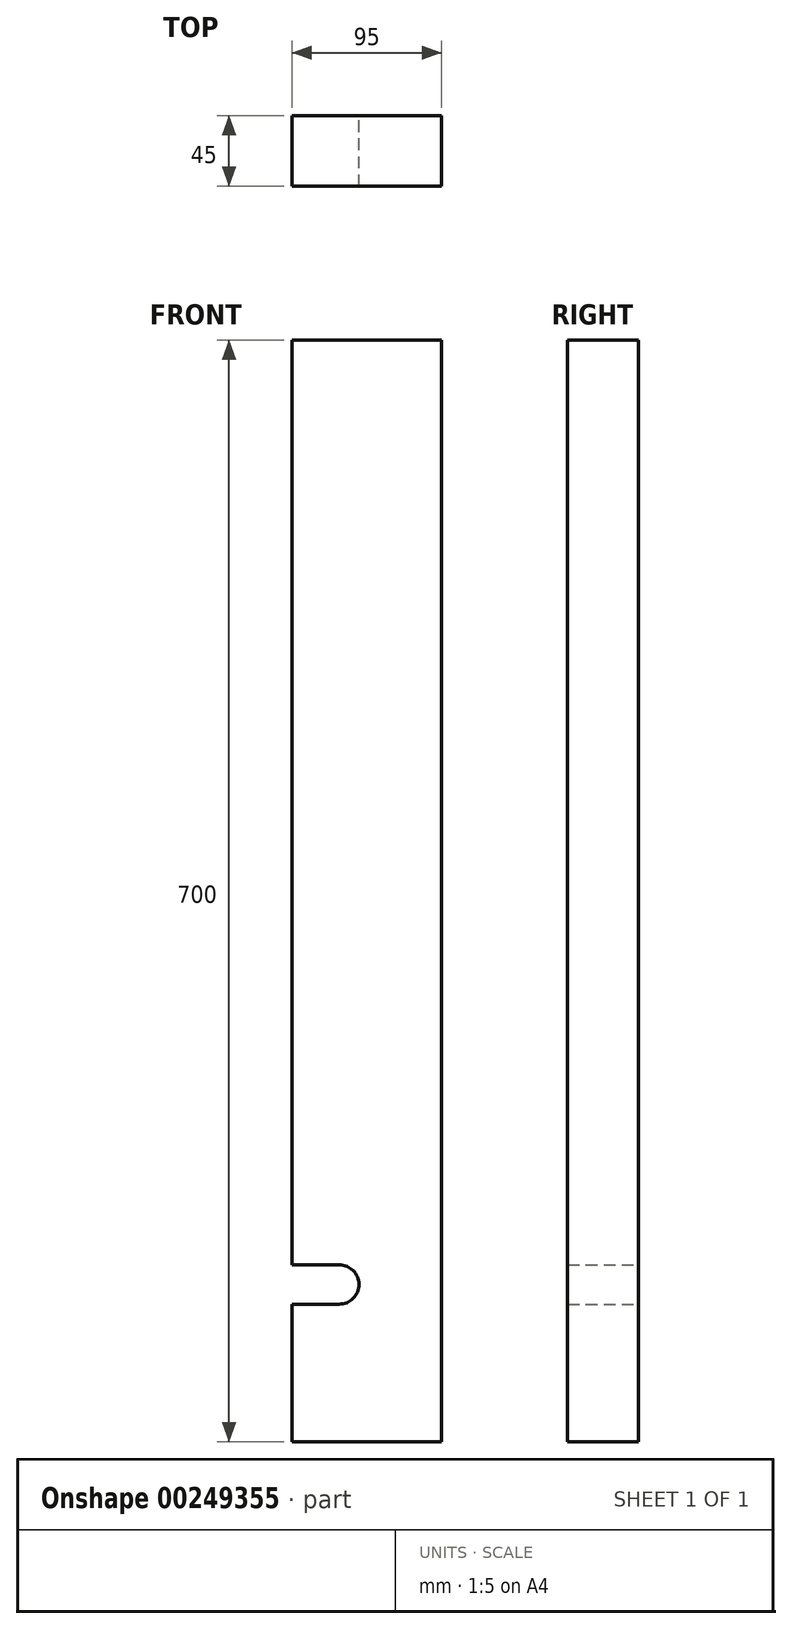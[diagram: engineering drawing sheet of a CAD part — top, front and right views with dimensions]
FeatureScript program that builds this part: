
annotation { "Feature Type Name" : "Feature", "Feature Type Description" : "" }
export const myFeature = defineFeature(function(context is Context, id is Id, definition is map)
    precondition{}
    {
        {
            var Q0;
            Q0=qCreatedBy(makeId("Front.planeOp"),FACE);
            var sketch = newSketch(context, id + "F0", { "sketchPlane" : qUnion([Q0])});
            skLineSegment(sketch, "E0.bottom", {"start": v(-47.5, 350) * mm, "end": v(47.5, 350) * mm});
            skLineSegment(sketch, "E0.top", {"start": v(-47.5, -350) * mm, "end": v(47.5, -350) * mm});
            skLineSegment(sketch, "E0.left", {"start": v(-47.5, 350) * mm, "end": v(-47.5, -237.5) * mm});
            skLineSegment(sketch, "E0.right", {"start": v(47.5, 350) * mm, "end": v(47.5, -350) * mm});
            skPoint(sketch, "E0.middle", {"position": v(0, 0) * mm});
            skArc(sketch, "E1", {"start": v(-17.5, -262.5) * mm, "mid": v(-5, -250) * mm, "end": v(-17.5, -237.5) * mm});
            skLineSegment(sketch, "E2", {"start": v(-47.5, -237.5) * mm, "end": v(-17.5, -237.5) * mm});
            skLineSegment(sketch, "E3", {"start": v(-47.5, -262.5) * mm, "end": v(-17.5, -262.5) * mm});
            skLineSegment(sketch, "E4.trimOffspring", {"start": v(-47.5, -262.5) * mm, "end": v(-47.5, -350) * mm});
            skSolve(sketch);
        }
        {
            var Q0;
            Q0 = qSketchRegion(id + "F0", true);
            extrude(context, id + "F1", {"entities" : qUnion([Q0]), "depth" : 45 * mm});
        }
    });
